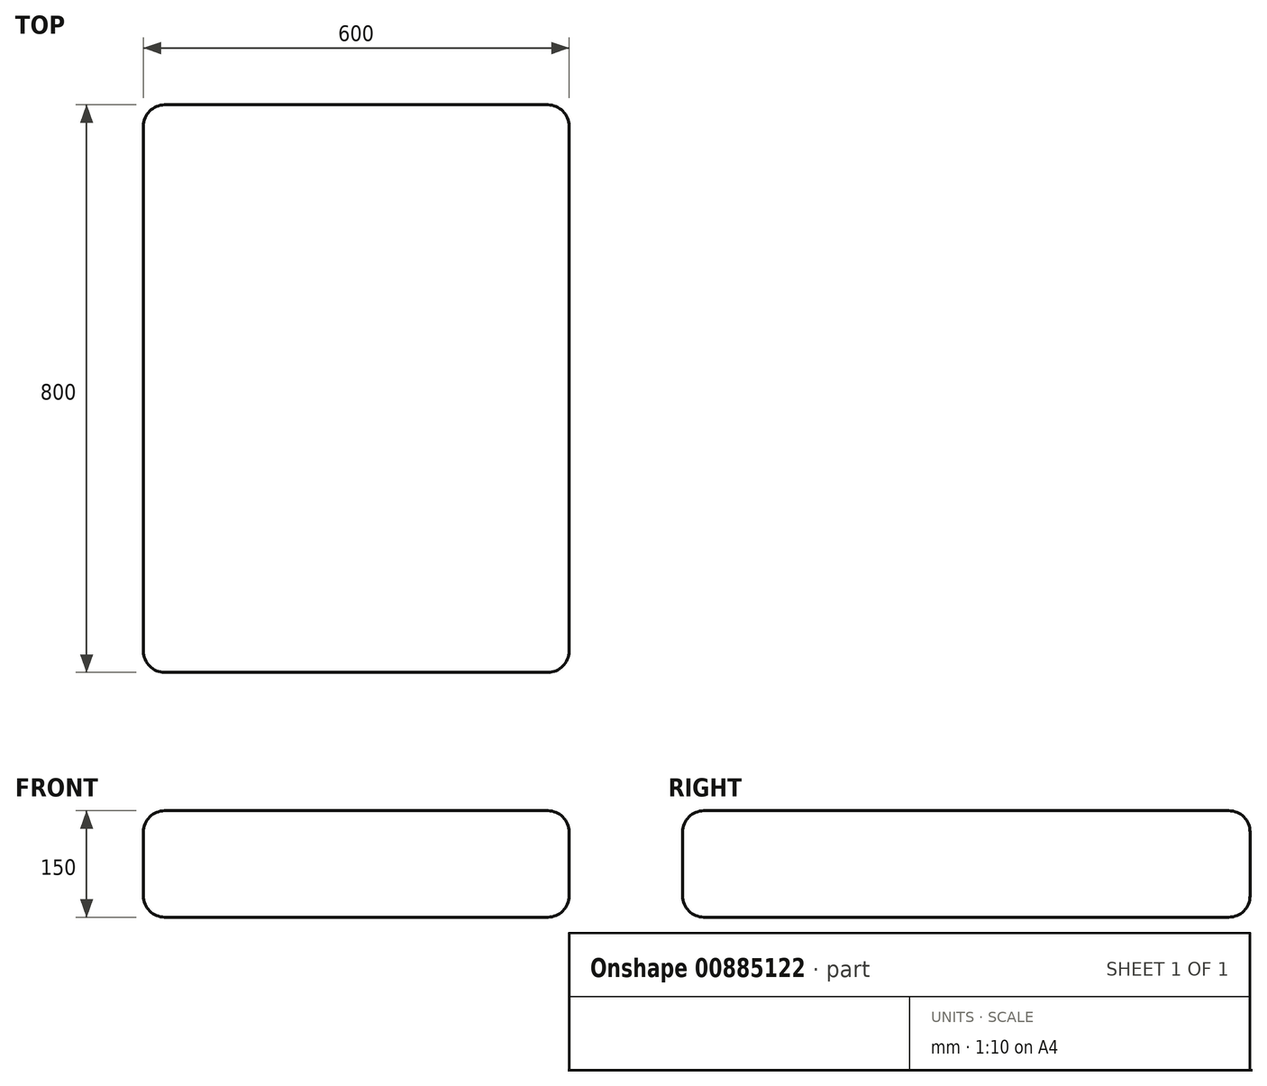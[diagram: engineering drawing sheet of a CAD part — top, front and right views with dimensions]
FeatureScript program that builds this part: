
annotation { "Feature Type Name" : "Feature", "Feature Type Description" : "" }
export const myFeature = defineFeature(function(context is Context, id is Id, definition is map)
    precondition{}
    {
        {
            var Q0;
            Q0=qCreatedBy(makeId("Top.planeOp"),FACE);
            var sketch = newSketch(context, id + "F0", { "sketchPlane" : qUnion([Q0])});
            skLineSegment(sketch, "E0.bottom", {"start": v(-300, 400) * mm, "end": v(300, 400) * mm});
            skLineSegment(sketch, "E0.top", {"start": v(-300, -400) * mm, "end": v(300, -400) * mm});
            skLineSegment(sketch, "E0.left", {"start": v(-300, 400) * mm, "end": v(-300, -400) * mm});
            skLineSegment(sketch, "E0.right", {"start": v(300, 400) * mm, "end": v(300, -400) * mm});
            skPoint(sketch, "E0.middle", {"position": v(0, 0) * mm});
            skSolve(sketch);
        }
        {
            var Q0;
            Q0=makeQuery(id+"F0.imprint","IMPRINT",FACE,{"disambiguationData":[TD([[makeQuery(id+"F0.imprint","IMPRINT",EDGE,{"derivedFrom":sQuery(id+"F0.wireOp",EDGE,"E0.bottom")}),-1.0]])]});
            extrude(context, id + "F1", {"entities" : qUnion([Q0]), "oppositeDirection" : true, "depth" : 150 * mm, "offsetDistance" : 25.4 * mm});
        }
        {
            var Q0;
            Q0=makeQuery(id+"F1.opExtrude","SWEPT_FACE",FACE,{"disambiguationData":[OSD([sQuery(id+"F0.wireOp",EDGE,"E0.bottom")])]});
            var Q1;
            Q1=makeQuery(id+"F1.opExtrude","SWEPT_FACE",FACE,{"disambiguationData":[OSD([sQuery(id+"F0.wireOp",EDGE,"E0.left")])]});
            var Q2;
            Q2=makeQuery(id+"F1.opExtrude","CAP_EDGE",EDGE,{"disambiguationData":[OSD([sQuery(id+"F0.wireOp",EDGE,"E0.top")])],"isStart":true});
            var Q3;
            Q3=makeQuery(id+"F1.opExtrude","CAP_EDGE",EDGE,{"disambiguationData":[OSD([sQuery(id+"F0.wireOp",EDGE,"E0.right")])],"isStart":true});
            var Q4;
            Q4=makeQuery(id+"F1.opExtrude","SWEPT_EDGE",EDGE,{"disambiguationData":[OSD([sQuery(id+"F0.wireOp",EDGE,"E0.top"),sQuery(id+"F0.wireOp",EDGE,"E0.right")])]});
            var Q5;
            Q5=makeQuery(id+"F1.opExtrude","SWEPT_FACE",FACE,{"disambiguationData":[OSD([sQuery(id+"F0.wireOp",EDGE,"E0.top")])]});
            var Q6;
            Q6=makeQuery(id+"F1.opExtrude","SWEPT_FACE",FACE,{"disambiguationData":[OSD([sQuery(id+"F0.wireOp",EDGE,"E0.right")])]});
            fillet(context, id + "F2", {"entities" : qUnion([Q0, Q1, Q2, Q3, Q4, Q5, Q6]), "radius" : 30 * mm, "tangentPropagation" : true, "allowEdgeOverflow" : false});
        }
    });
